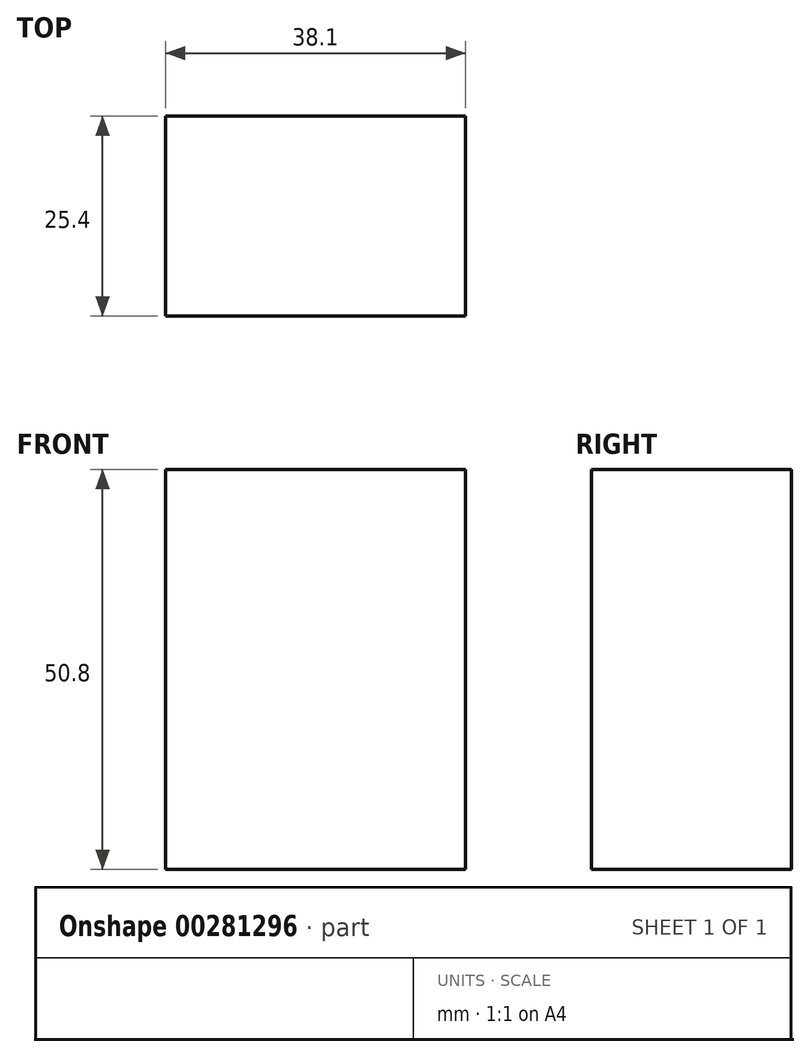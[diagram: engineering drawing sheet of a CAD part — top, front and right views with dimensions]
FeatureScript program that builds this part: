
annotation { "Feature Type Name" : "Feature", "Feature Type Description" : "" }
export const myFeature = defineFeature(function(context is Context, id is Id, definition is map)
    precondition{}
    {
        {
            var Q0;
            Q0=qCreatedBy(makeId("Front.planeOp"),FACE);
            var sketch = newSketch(context, id + "F0", { "sketchPlane" : qUnion([Q0])});
            skLineSegment(sketch, "E0.bottom", {"start": v(-51.48, 36.34) * mm, "end": v(-13.38, 36.34) * mm});
            skLineSegment(sketch, "E0.top", {"start": v(-51.48, -14.46) * mm, "end": v(-13.38, -14.46) * mm});
            skLineSegment(sketch, "E0.left", {"start": v(-51.48, 36.34) * mm, "end": v(-51.48, -14.46) * mm});
            skLineSegment(sketch, "E0.right", {"start": v(-13.38, 36.34) * mm, "end": v(-13.38, -14.46) * mm});
            skSolve(sketch);
        }
        {
            var Q0;
            Q0 = qSketchRegion(id + "F0", true);
            extrude(context, id + "F1", {"entities" : qUnion([Q0]), "depth" : 25.4 * mm});
        }
    });
